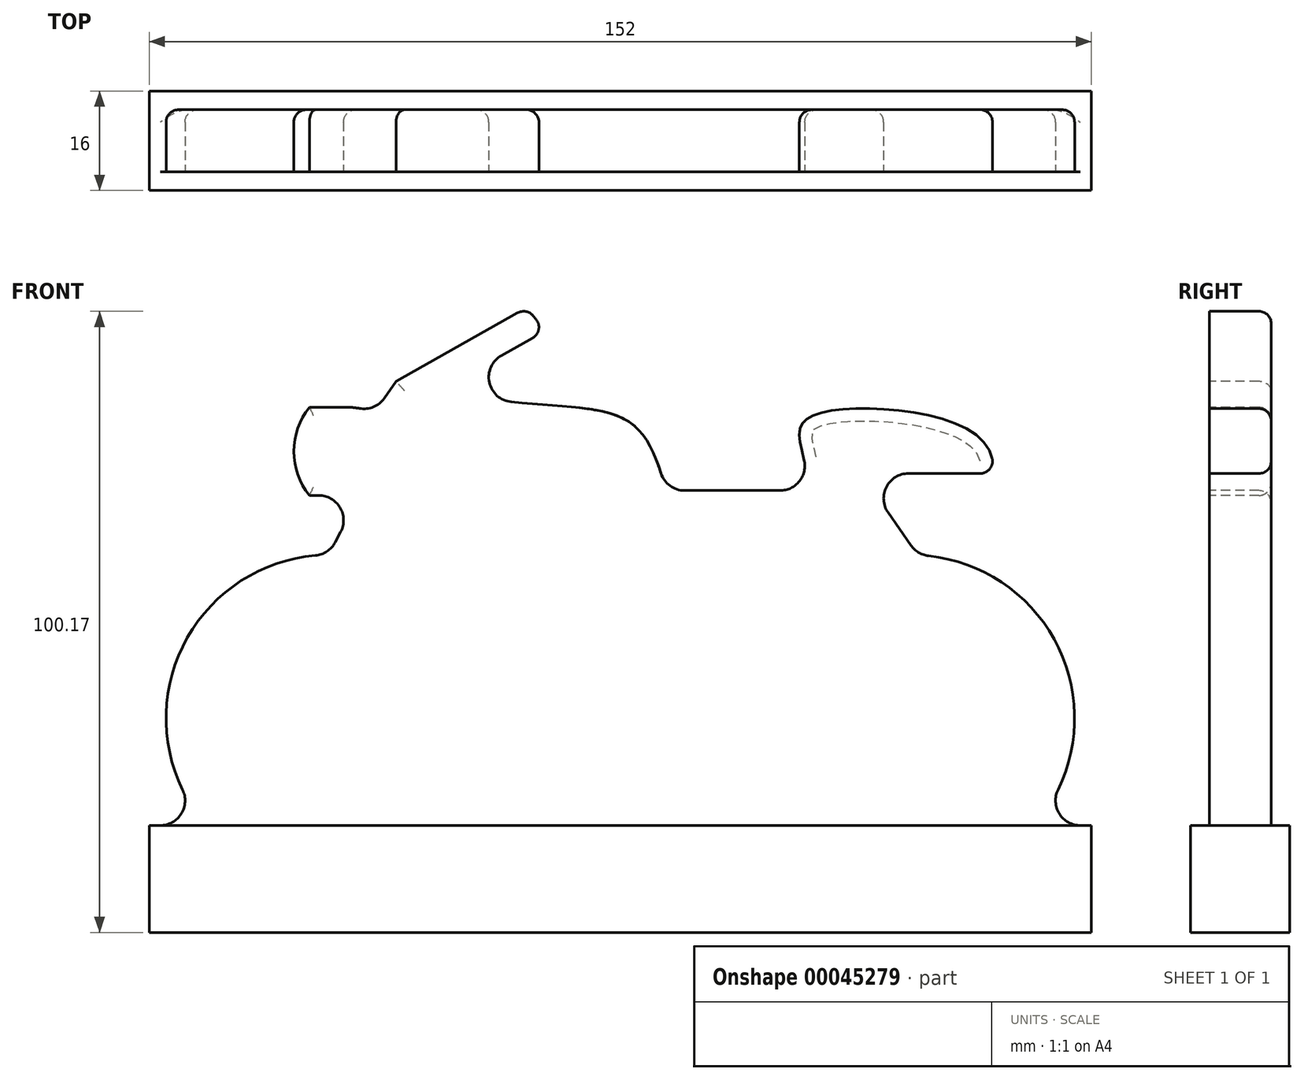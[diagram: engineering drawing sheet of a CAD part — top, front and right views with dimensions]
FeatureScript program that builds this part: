
annotation { "Feature Type Name" : "Feature", "Feature Type Description" : "" }
export const myFeature = defineFeature(function(context is Context, id is Id, definition is map)
    precondition{}
    {
        {
            var Q0;
            Q0=qCreatedBy(makeId("Front.planeOp"),FACE);
            var sketch = newSketch(context, id + "F0", { "sketchPlane" : qUnion([Q0])});
            skLineSegment(sketch, "E0.rect.bottom", {"start": v(76, 59) * mm, "end": v(-76, 59) * mm});
            skLineSegment(sketch, "E0.rect.top", {"start": v(76, -59) * mm, "end": v(-76, -59) * mm});
            skLineSegment(sketch, "E0.rect.left", {"start": v(76, 59) * mm, "end": v(76, -59) * mm});
            skLineSegment(sketch, "E0.rect.right", {"start": v(-76, 59) * mm, "end": v(-76, -59) * mm});
            skPoint(sketch, "E0.rect.middle", {"position": v(0, 0) * mm});
            skSolve(sketch);
        }
        {
            var Q0;
            Q0 = qSketchRegion(id + "F0", true);
            extrude(context, id + "F1", {"entities" : qUnion([Q0]), "depth" : 10 * mm});
        }
        {
            var Q0;
            Q0=makeQuery(id+"F1.opExtrude","CAP_FACE",FACE,{"disambiguationData":[OSD([sQuery(id+"F0.wireOp",EDGE,"E0.rect.bottom"),sQuery(id+"F0.wireOp",EDGE,"E0.rect.top"),sQuery(id+"F0.wireOp",EDGE,"E0.rect.left"),sQuery(id+"F0.wireOp",EDGE,"E0.rect.right")])],"isStart":false});
            var sketch = newSketch(context, id + "F2", { "sketchPlane" : qUnion([Q0])});
            skArc(sketch, "E1", {"start": v(-49.2, 1.78) * mm, "mid": v(-69.85, -11.46) * mm, "end": v(-70.62, -35.98) * mm});
            skArc(sketch, "E2", {"start": v(70.62, -35.98) * mm, "mid": v(69.99, -11.7) * mm, "end": v(49.74, 1.73) * mm});
            skLineSegment(sketch, "E3", {"start": v(0, 75.36) * mm, "end": v(0, -68.44) * mm, "construction": true});
            skPoint(sketch, "E3.endSnap0", {"position": v(0, -59) * mm});
            skLineSegment(sketch, "E4", {"start": v(13.49, -20.6) * mm, "end": v(13.46, -20.47) * mm});
            skLineSegment(sketch, "E5", {"start": v(10.36, 12.26) * mm, "end": v(25.77, 12.26) * mm});
            skFitSpline(sketch, "E6", {"points": [v(59.66, 15.01) * mm, v(58.03, 20.7) * mm, v(40.67, 25.47) * mm, v(29.84, 23.64) * mm, v(29, 20.2) * mm, v(30.37, 12.3) * mm], "startDerivative": vector(17.26, 24.94) * mm, "endDerivative": vector(-3.19, -34) * mm});
            skPoint(sketch, "E7.newPointA", {"position": v(30.37, 12.26) * mm});
            skArc(sketch, "E7.filletArc", {"start": v(25.77, 12.26) * mm, "mid": v(28.91, 13.79) * mm, "end": v(29.65, 17.2) * mm});
            skLineSegment(sketch, "E8.trimOffspring", {"start": v(46.48, 15.01) * mm, "end": v(59.66, 15.01) * mm});
            skPoint(sketch, "E9.orphan", {"position": v(-62.5, 25.33) * mm});
            skPoint(sketch, "E10.orphan", {"position": v(5.32, 12.26) * mm});
            skLineSegment(sketch, "E11", {"start": v(-76, -41.74) * mm, "end": v(-74.21, -41.74) * mm});
            skLineSegment(sketch, "E12.trimOffspring", {"start": v(74.21, -41.74) * mm, "end": v(76, -41.74) * mm});
            skPoint(sketch, "E13.start.orphan", {"position": v(-48.06, 0) * mm});
            skPoint(sketch, "E14.3.internal.snap0", {"position": v(-34.76, 12.2) * mm});
            skPoint(sketch, "E14.4.internal.snap0", {"position": v(-34.76, 12.2) * mm});
            skFitSpline(sketch, "E14", {"points": [v(7.38, 12.26) * mm, v(1.9, 23) * mm, v(-13.97, 26.23) * mm, v(-34.76, 25.24) * mm, v(-34.76, 12.26) * mm], "startDerivative": vector(-16.94, 59.52) * mm, "endDerivative": vector(17.38, -70.71) * mm});
            skLineSegment(sketch, "E15", {"start": v(-46, 3.9) * mm, "end": v(-45.1, 5.6) * mm});
            skLineSegment(sketch, "E16", {"start": v(46.89, 3.42) * mm, "end": v(43.2, 8.73) * mm});
            skLineSegment(sketch, "E17", {"start": v(-50.15, 25.69) * mm, "end": v(-44.05, 25.69) * mm});
            skArc(sketch, "E18", {"start": v(-42.08, 25.5) * mm, "mid": v(-43.06, 25.64) * mm, "end": v(-44.05, 25.69) * mm});
            skPoint(sketch, "E19.visualSharp", {"position": v(-42.5, 10.55) * mm});
            skArc(sketch, "E19.filletArc", {"start": v(-45.1, 5.6) * mm, "mid": v(-45.22, 9.54) * mm, "end": v(-48.65, 11.47) * mm});
            skArc(sketch, "E20.filletArc", {"start": v(6.55, 15.04) * mm, "mid": v(8, 13.03) * mm, "end": v(10.36, 12.26) * mm});
            skPoint(sketch, "E21.visualSharp", {"position": v(-47.07, 1.88) * mm});
            skArc(sketch, "E21.filletArc", {"start": v(-49.2, 1.78) * mm, "mid": v(-47.33, 2.44) * mm, "end": v(-46, 3.9) * mm});
            skPoint(sketch, "E22.visualSharp", {"position": v(47.97, 1.86) * mm});
            skArc(sketch, "E22.filletArc", {"start": v(46.89, 3.42) * mm, "mid": v(48.13, 2.27) * mm, "end": v(49.74, 1.73) * mm});
            skPoint(sketch, "E23.visualSharp", {"position": v(-66.8, -41.74) * mm});
            skArc(sketch, "E23.filletArc", {"start": v(-74.21, -41.74) * mm, "mid": v(-70.82, -39.86) * mm, "end": v(-70.62, -35.98) * mm});
            skPoint(sketch, "E24.visualSharp", {"position": v(66.8, -41.74) * mm});
            skArc(sketch, "E24.filletArc", {"start": v(70.62, -35.98) * mm, "mid": v(70.82, -39.86) * mm, "end": v(74.21, -41.74) * mm});
            skPoint(sketch, "E25.visualSharp", {"position": v(-36.19, 22.3) * mm});
            skPoint(sketch, "E26.visualSharp", {"position": v(38.82, 15.01) * mm});
            skArc(sketch, "E26.filletArc", {"start": v(46.48, 15.01) * mm, "mid": v(42.93, 12.87) * mm, "end": v(43.2, 8.73) * mm});
            skLineSegment(sketch, "E27", {"start": v(-38.07, 27.14) * mm, "end": v(-36.17, 29.85) * mm});
            skLineSegment(sketch, "E28", {"start": v(-36.17, 29.85) * mm, "end": v(-15.12, 41.73) * mm});
            skLineSegment(sketch, "E29", {"start": v(-15.12, 41.73) * mm, "end": v(-12.07, 38.05) * mm});
            skLineSegment(sketch, "E30", {"start": v(-12.07, 38.05) * mm, "end": v(-19.19, 34.03) * mm});
            skFitSpline(sketch, "E31.trimOffspring", {"points": [v(7.38, 12.26) * mm, v(1.9, 23) * mm, v(-13.97, 26.23) * mm, v(-34.76, 25.24) * mm, v(-34.76, 12.26) * mm], "startDerivative": vector(-16.94, 59.52) * mm, "endDerivative": vector(17.38, -70.71) * mm});
            skPoint(sketch, "E32.visualSharp", {"position": v(-32.78, 26.36) * mm});
            skArc(sketch, "E32.filletArc", {"start": v(-19.19, 34.03) * mm, "mid": v(-21.13, 29.7) * mm, "end": v(-17.6, 26.56) * mm});
            skLineSegment(sketch, "E33", {"start": v(-76, -41.74) * mm, "end": v(-76, 59) * mm});
            skLineSegment(sketch, "E34", {"start": v(-76, 59) * mm, "end": v(76, 59) * mm});
            skLineSegment(sketch, "E35", {"start": v(76, 59) * mm, "end": v(76, -41.74) * mm});
            skLineSegment(sketch, "E36", {"start": v(-48.65, 11.47) * mm, "end": v(-50.15, 11.47) * mm});
            skArc(sketch, "E37", {"start": v(-50.15, 25.69) * mm, "mid": v(-52.66, 18.58) * mm, "end": v(-50.15, 11.47) * mm});
            skPoint(sketch, "E38.visualSharp", {"position": v(-39.72, 24.78) * mm});
            skArc(sketch, "E38.filletArc", {"start": v(-42.08, 25.5) * mm, "mid": v(-39.83, 25.74) * mm, "end": v(-38.07, 27.14) * mm});
            skSolve(sketch);
        }
        {
            var Q0;
            Q0=makeQuery(id+"F2.imprint","IMPRINT",FACE,{"disambiguationData":[TD([[makeQuery(id+"F2.imprint","IMPRINT",EDGE,{"derivedFrom":sQuery(id+"F2.wireOp",EDGE,"E1")}),-1.0]])]});
            extrude(context, id + "F3", {"entities" : qUnion([Q0]), "operationType" : NewBodyOperationType.REMOVE, "endBound" : BoundingType.THROUGH_ALL, "oppositeDirection" : true, "depth" : 25 * mm});
        }
        {
            var Q0;
            Q0=makeQuery(id+"F1.opExtrude","CAP_FACE",FACE,{"disambiguationData":[OSD([sQuery(id+"F0.wireOp",EDGE,"E0.rect.bottom"),sQuery(id+"F0.wireOp",EDGE,"E0.rect.top"),sQuery(id+"F0.wireOp",EDGE,"E0.rect.left"),sQuery(id+"F0.wireOp",EDGE,"E0.rect.right")])],"isStart":false});
            var Q1;
            Q1=makeQuery(id+"F1.opExtrude","CAP_FACE",FACE,{"disambiguationData":[OSD([sQuery(id+"F0.wireOp",EDGE,"E0.rect.bottom"),sQuery(id+"F0.wireOp",EDGE,"E0.rect.top"),sQuery(id+"F0.wireOp",EDGE,"E0.rect.left"),sQuery(id+"F0.wireOp",EDGE,"E0.rect.right")])],"isStart":true});
            cPlane(context, id + "F4", {"entities" : qUnion([Q0, Q1]), "cplaneType" : CPlaneType.MID_PLANE, "offset" : 150 * mm, "width" : 150 * mm, "height" : 150 * mm});
        }
        {
            var Q0;
            Q0=qCreatedBy(id+"F4.planeOp",FACE);
            var sketch = newSketch(context, id + "F5", { "sketchPlane" : qUnion([Q0])});
            skLineSegment(sketch, "E39.0", {"start": v(-76, -41.74) * mm, "end": v(-76, -59) * mm});
            skLineSegment(sketch, "E39.1", {"start": v(76, -59) * mm, "end": v(-76, -59) * mm});
            skLineSegment(sketch, "E39.2", {"start": v(76, -41.74) * mm, "end": v(76, -59) * mm});
            skLineSegment(sketch, "E40", {"start": v(-76, -41.74) * mm, "end": v(76, -41.74) * mm});
            skSolve(sketch);
        }
        {
            var Q0;
            Q0 = qSketchRegion(id + "F5", true);
            extrude(context, id + "F6", {"entities" : qUnion([Q0]), "operationType" : NewBodyOperationType.ADD, "depth" : 8 * mm, "hasSecondDirection" : true, "secondDirectionOppositeDirection" : true, "secondDirectionDepth" : 8 * mm});
        }
        {
            var Q0;
            Q0=makeQuery(id+"F1.opExtrude","CAP_FACE",FACE,{"disambiguationData":[OSD([sQuery(id+"F0.wireOp",EDGE,"E0.rect.bottom"),sQuery(id+"F0.wireOp",EDGE,"E0.rect.top"),sQuery(id+"F0.wireOp",EDGE,"E0.rect.left"),sQuery(id+"F0.wireOp",EDGE,"E0.rect.right")])],"isStart":false});
            var sketch = newSketch(context, id + "F7", { "sketchPlane" : qUnion([Q0])});
            skArc(sketch, "E41.0", {"start": v(-49.2, 1.78) * mm, "mid": v(-69.85, -11.46) * mm, "end": v(-70.62, -35.98) * mm, "construction": true});
            skCircle(sketch, "E42", {"center": v(-46.95, -24.45) * mm, "radius": 14.33 * mm});
            skArc(sketch, "E43.0", {"start": v(70.62, -35.98) * mm, "mid": v(69.99, -11.7) * mm, "end": v(49.74, 1.73) * mm, "construction": true});
            skCircle(sketch, "E44", {"center": v(46.95, -24.45) * mm, "radius": 14.33 * mm});
            skCircle(sketch, "E45", {"center": v(-46.95, -24.45) * mm, "radius": 4.36 * mm});
            skCircle(sketch, "E46", {"center": v(46.95, -24.45) * mm, "radius": 5.44 * mm});
            skLineSegment(sketch, "E47", {"start": v(-46.95, -24.45) * mm, "end": v(-34.7, 21.51) * mm});
            skLineSegment(sketch, "E48", {"start": v(-34.7, 21.51) * mm, "end": v(8, 6.65) * mm});
            skPoint(sketch, "E48.endSnap0", {"position": v(8, 13.03) * mm});
            skLineSegment(sketch, "E49", {"start": v(8, 6.65) * mm, "end": v(18.47, -21.29) * mm});
            skLineSegment(sketch, "E50", {"start": v(18.47, -21.29) * mm, "end": v(12.84, -26.92) * mm});
            skLineSegment(sketch, "E51", {"start": v(12.84, -26.92) * mm, "end": v(-14.64, -26.92) * mm});
            skArc(sketch, "E52", {"start": v(-22.75, -21.74) * mm, "mid": v(-19.45, -25.51) * mm, "end": v(-14.64, -26.92) * mm});
            skLineSegment(sketch, "E53", {"start": v(-22.75, -21.74) * mm, "end": v(-37.65, 10.43) * mm});
            skLineSegment(sketch, "E54", {"start": v(18.47, -21.29) * mm, "end": v(32.46, 6.65) * mm});
            skLineSegment(sketch, "E55", {"start": v(8.79, 6.65) * mm, "end": v(32.46, 6.65) * mm});
            skLineSegment(sketch, "E56", {"start": v(46.95, -24.45) * mm, "end": v(32.46, 6.65) * mm});
            skLineSegment(sketch, "E57", {"start": v(18.47, -21.29) * mm, "end": v(46.95, -24.45) * mm});
            skLineSegment(sketch, "E58", {"start": v(32.46, 6.65) * mm, "end": v(38.75, 6.65) * mm});
            skCircle(sketch, "E59", {"center": v(-46.95, -24.45) * mm, "radius": 26.33 * mm});
            skPoint(sketch, "E59.third.point", {"position": v(-21.76, -32.13) * mm});
            skCircle(sketch, "E60", {"center": v(46.95, -24.45) * mm, "radius": 26.33 * mm});
            skFitSpline(sketch, "E61", {"points": [v(47.34, -19.02) * mm, v(48.56, -14.29) * mm, v(48.93, -10.26) * mm], "startDerivative": vector(3, 6.36) * mm, "endDerivative": vector(-1.27, 8.66) * mm});
            skLineSegment(sketch, "E62", {"start": v(48.42, -19.2) * mm, "end": v(50.82, -10.65) * mm, "construction": true});
            skFitSpline(sketch, "E63.MirrorCS", {"points": [v(49.44, -19.6) * mm, v(50.86, -14.93) * mm, v(52.64, -11.3) * mm], "startDerivative": vector(0.76, 6.99) * mm, "endDerivative": vector(5.6, 6.73) * mm});
            skPoint(sketch, "E64", {"position": v(49.62, -14.93) * mm});
            skSolve(sketch);
        }
        {
            var Q0;
            Q0=makeQuery(id+"F3.boolean.opBoolean","COPY",EDGE,{"derivedFrom":makeQuery(id+"F3.opExtrude","SWEPT_EDGE",EDGE,{"disambiguationData":[OSD([sQuery(id+"F2.wireOp",EDGE,"E6"),sQuery(id+"F2.wireOp",EDGE,"E8.trimOffspring")])]})});
            var Q1;
            Q1=makeQuery(id+"F3.boolean.opBoolean","INTERSECT",EDGE,{"derivedFrom":[makeQuery(id+"F1.opExtrude","CAP_FACE",FACE,{"disambiguationData":[OSD([sQuery(id+"F0.wireOp",EDGE,"E0.rect.bottom"),sQuery(id+"F0.wireOp",EDGE,"E0.rect.top"),sQuery(id+"F0.wireOp",EDGE,"E0.rect.left"),sQuery(id+"F0.wireOp",EDGE,"E0.rect.right")])],"isStart":true}),makeQuery(id+"F3.opExtrude","SWEPT_FACE",FACE,{"disambiguationData":[OSD([sQuery(id+"F2.wireOp",EDGE,"E8.trimOffspring")])]})]});
            var Q2;
            Q2=makeQuery(id+"F3.boolean.opBoolean","INTERSECT",EDGE,{"derivedFrom":[makeQuery(id+"F1.opExtrude","CAP_FACE",FACE,{"disambiguationData":[OSD([sQuery(id+"F0.wireOp",EDGE,"E0.rect.bottom"),sQuery(id+"F0.wireOp",EDGE,"E0.rect.top"),sQuery(id+"F0.wireOp",EDGE,"E0.rect.left"),sQuery(id+"F0.wireOp",EDGE,"E0.rect.right")])],"isStart":true}),makeQuery(id+"F3.opExtrude","SWEPT_FACE",FACE,{"disambiguationData":[OSD([sQuery(id+"F2.wireOp",EDGE,"E6")])]})]});
            var Q3;
            Q3=makeQuery(id+"F3.boolean.opBoolean","INTERSECT",EDGE,{"derivedFrom":[makeQuery(id+"F1.opExtrude","CAP_FACE",FACE,{"disambiguationData":[OSD([sQuery(id+"F0.wireOp",EDGE,"E0.rect.bottom"),sQuery(id+"F0.wireOp",EDGE,"E0.rect.top"),sQuery(id+"F0.wireOp",EDGE,"E0.rect.left"),sQuery(id+"F0.wireOp",EDGE,"E0.rect.right")])],"isStart":true}),makeQuery(id+"F3.opExtrude","SWEPT_FACE",FACE,{"disambiguationData":[OSD([sQuery(id+"F2.wireOp",EDGE,"E29")])]})]});
            var Q4;
            Q4=makeQuery(id+"F3.boolean.opBoolean","INTERSECT",EDGE,{"derivedFrom":[makeQuery(id+"F1.opExtrude","CAP_FACE",FACE,{"disambiguationData":[OSD([sQuery(id+"F0.wireOp",EDGE,"E0.rect.bottom"),sQuery(id+"F0.wireOp",EDGE,"E0.rect.top"),sQuery(id+"F0.wireOp",EDGE,"E0.rect.left"),sQuery(id+"F0.wireOp",EDGE,"E0.rect.right")])],"isStart":true}),makeQuery(id+"F3.opExtrude","SWEPT_FACE",FACE,{"disambiguationData":[OSD([sQuery(id+"F2.wireOp",EDGE,"E28")])]})]});
            var Q5;
            Q5=makeQuery(id+"F3.boolean.opBoolean","INTERSECT",EDGE,{"derivedFrom":[makeQuery(id+"F1.opExtrude","CAP_FACE",FACE,{"disambiguationData":[OSD([sQuery(id+"F0.wireOp",EDGE,"E0.rect.bottom"),sQuery(id+"F0.wireOp",EDGE,"E0.rect.top"),sQuery(id+"F0.wireOp",EDGE,"E0.rect.left"),sQuery(id+"F0.wireOp",EDGE,"E0.rect.right")])],"isStart":true}),makeQuery(id+"F3.opExtrude","SWEPT_FACE",FACE,{"disambiguationData":[OSD([sQuery(id+"F2.wireOp",EDGE,"E17")])]})]});
            var Q6;
            Q6=makeQuery(id+"F3.boolean.opBoolean","INTERSECT",EDGE,{"derivedFrom":[makeQuery(id+"F1.opExtrude","CAP_FACE",FACE,{"disambiguationData":[OSD([sQuery(id+"F0.wireOp",EDGE,"E0.rect.bottom"),sQuery(id+"F0.wireOp",EDGE,"E0.rect.top"),sQuery(id+"F0.wireOp",EDGE,"E0.rect.left"),sQuery(id+"F0.wireOp",EDGE,"E0.rect.right")])],"isStart":true}),makeQuery(id+"F3.opExtrude","SWEPT_FACE",FACE,{"disambiguationData":[OSD([sQuery(id+"F2.wireOp",EDGE,"E37")])]})]});
            var Q7;
            Q7=makeQuery(id+"F3.boolean.opBoolean","INTERSECT",EDGE,{"derivedFrom":[makeQuery(id+"F1.opExtrude","CAP_FACE",FACE,{"disambiguationData":[OSD([sQuery(id+"F0.wireOp",EDGE,"E0.rect.bottom"),sQuery(id+"F0.wireOp",EDGE,"E0.rect.top"),sQuery(id+"F0.wireOp",EDGE,"E0.rect.left"),sQuery(id+"F0.wireOp",EDGE,"E0.rect.right")])],"isStart":true}),makeQuery(id+"F3.opExtrude","SWEPT_FACE",FACE,{"disambiguationData":[OSD([sQuery(id+"F2.wireOp",EDGE,"E19.filletArc")])]})]});
            var Q8;
            Q8=makeQuery(id+"F3.boolean.opBoolean","COPY",EDGE,{"derivedFrom":makeQuery(id+"F3.opExtrude","CAP_EDGE",EDGE,{"disambiguationData":[OSD([sQuery(id+"F2.wireOp",EDGE,"E2")])],"isStart":true})});
            var Q9;
            Q9=makeQuery(id+"F3.boolean.opBoolean","COPY",EDGE,{"derivedFrom":makeQuery(id+"F3.opExtrude","CAP_EDGE",EDGE,{"disambiguationData":[OSD([sQuery(id+"F2.wireOp",EDGE,"E6")])],"isStart":true})});
            var Q10;
            Q10=makeQuery(id+"F3.boolean.opBoolean","COPY",EDGE,{"derivedFrom":makeQuery(id+"F3.opExtrude","CAP_EDGE",EDGE,{"disambiguationData":[OSD([sQuery(id+"F2.wireOp",EDGE,"E29")])],"isStart":true})});
            var Q11;
            Q11=makeQuery(id+"F3.boolean.opBoolean","COPY",EDGE,{"derivedFrom":makeQuery(id+"F3.opExtrude","SWEPT_EDGE",EDGE,{"disambiguationData":[OSD([sQuery(id+"F2.wireOp",EDGE,"E28"),sQuery(id+"F2.wireOp",EDGE,"E29")])]})});
            var Q12;
            Q12=makeQuery(id+"F3.boolean.opBoolean","COPY",EDGE,{"derivedFrom":makeQuery(id+"F3.opExtrude","SWEPT_EDGE",EDGE,{"disambiguationData":[OSD([sQuery(id+"F2.wireOp",EDGE,"E29"),sQuery(id+"F2.wireOp",EDGE,"E30")])]})});
            var Q13;
            Q13=makeQuery(id+"F3.boolean.opBoolean","COPY",EDGE,{"derivedFrom":makeQuery(id+"F3.opExtrude","CAP_EDGE",EDGE,{"disambiguationData":[OSD([sQuery(id+"F2.wireOp",EDGE,"E28")])],"isStart":true})});
            var Q14;
            Q14=makeQuery(id+"F3.boolean.opBoolean","COPY",EDGE,{"derivedFrom":makeQuery(id+"F3.opExtrude","CAP_EDGE",EDGE,{"disambiguationData":[OSD([sQuery(id+"F2.wireOp",EDGE,"E27")])],"isStart":true})});
            var Q15;
            Q15=makeQuery(id+"F3.boolean.opBoolean","COPY",EDGE,{"derivedFrom":makeQuery(id+"F3.opExtrude","CAP_EDGE",EDGE,{"disambiguationData":[OSD([sQuery(id+"F2.wireOp",EDGE,"E18")])],"isStart":true})});
            var Q16;
            Q16=makeQuery(id+"F3.boolean.opBoolean","COPY",EDGE,{"derivedFrom":makeQuery(id+"F3.opExtrude","CAP_EDGE",EDGE,{"disambiguationData":[OSD([sQuery(id+"F2.wireOp",EDGE,"E37")])],"isStart":true})});
            var Q17;
            Q17=makeQuery(id+"F3.boolean.opBoolean","COPY",EDGE,{"derivedFrom":makeQuery(id+"F3.opExtrude","CAP_EDGE",EDGE,{"disambiguationData":[OSD([sQuery(id+"F2.wireOp",EDGE,"E19.filletArc")])],"isStart":true})});
            var Q18;
            Q18=makeQuery(id+"F3.boolean.opBoolean","COPY",EDGE,{"derivedFrom":makeQuery(id+"F3.opExtrude","CAP_EDGE",EDGE,{"disambiguationData":[OSD([sQuery(id+"F2.wireOp",EDGE,"E1")])],"isStart":true})});
            fillet(context, id + "F8", {"entities" : qUnion([Q0, Q1, Q2, Q3, Q4, Q5, Q6, Q7, Q8, Q9, Q10, Q11, Q12, Q13, Q14, Q15, Q16, Q17, Q18]), "radius" : 2 * mm, "tangentPropagation" : true, "allowEdgeOverflow" : false});
        }
    });
